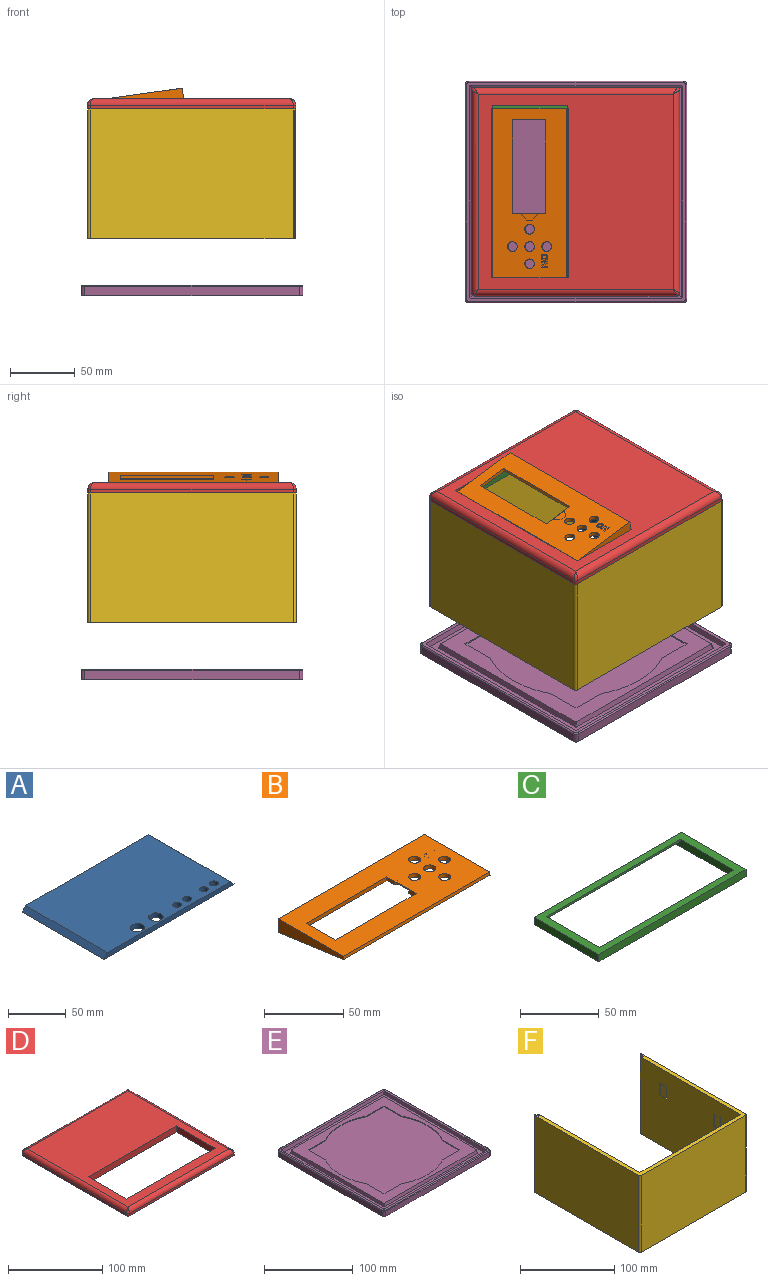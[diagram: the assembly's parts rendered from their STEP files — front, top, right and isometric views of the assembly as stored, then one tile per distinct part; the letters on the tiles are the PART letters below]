
ASSEMBLY  parts=6 mates=5
PART A: 20 faces, bbox 159.9x100x5 mm
  f0: plane 158.7x100mm, normal (0,0,-1), area 15455.6mm2, adj f2,f3,f4,f6,f8,f9,f10,f11
  f1: plane 150.52x100mm, normal (0,0,1), area 14637.8mm2, adj f3,f4,f5,f7,f8,f9,f10,f11
  f2: cylinder r=1mm len=100mm, axis (0,-1,0), area 68.3mm2, adj f0,f3,f4,f7
  f3: plane 159.91x4.98mm, normal (0,1,0), area 774.5mm2, adj f0,f1,f2,f5,f6,f7
  f4: plane 159.91x4.98mm, normal (0,-1,0), area 774.5mm2, adj f0,f1,f2,f5,f6,f7
  f5: plane 100x4.69mm, normal (-0.71,0,0.71), area 663.9mm2, adj f1,f3,f4,f6
  f6: cylinder r=1mm len=100mm, axis (0,-1,0), area 68.3mm2, adj f0,f3,f4,f5
  f7: plane 100x4.69mm, normal (0.71,0,0.71), area 663.9mm2, adj f1,f2,f3,f4
  f8: cylinder r=3.72mm len=7.44mm, axis (0,0,-1), area 116.4mm2, adj f0,f1
  f9: plane 5.37x4.98mm, normal (0,-1,0), area 26.7mm2, adj f0,f1,f10,f12
  f10: cylinder r=6.3mm len=11.4mm, axis (0,0,-1), area 71mm2, adj f0,f1,f9,f11
  f11: plane 5.37x4.98mm, normal (0,1,0), area 26.7mm2, adj f0,f1,f10,f12
  f12: cylinder r=6.3mm len=11.4mm, axis (0,0,-1), area 71mm2, adj f0,f1,f9,f11
  f13: plane 5.37x4.98mm, normal (0,1,0), area 26.7mm2, adj f0,f1,f14,f16
  f14: cylinder r=6.3mm len=11.4mm, axis (0,0,-1), area 71mm2, adj f0,f1,f13,f15
  f15: plane 5.37x4.98mm, normal (0,-1,0), area 26.7mm2, adj f0,f1,f14,f16
  f16: cylinder r=6.3mm len=11.4mm, axis (0,0,-1), area 71mm2, adj f0,f1,f13,f15
  f17: cylinder r=3.72mm len=7.44mm, axis (0,0,-1), area 116.4mm2, adj f0,f1
  f18: cylinder r=3.72mm len=7.44mm, axis (0,0,-1), area 116.4mm2, adj f0,f1
  f19: cylinder r=3.72mm len=7.44mm, axis (0,0,-1), area 116.4mm2, adj f0,f1
PART B: 69 faces, bbox 130.7x58.8x10.5 mm
  f0: plane 122.65x49.1mm, normal (0,0,-1), area 3728.6mm2, adj f3,f4,f5,f6,f7,f8,f9,f10
  f1: plane 58.44x10.54mm, normal (1,0,0), area 376.1mm2, adj f2,f17,f57,f59,f60,f61
  f2: plane 130.65x7.55mm, normal (0,1,0), area 986.6mm2, adj f1,f17,f56,f61
  f3: plane 49.1x6.97mm, normal (1,0,0), area 173.6mm2, adj f0,f4,f7,f57
  f4: plane 122.65x6.97mm, normal (0,-1,0), area 854.9mm2, adj f0,f3,f5,f57
  f5: plane 6.97x1mm, normal (-1,0,0), area 6.9mm2, adj f0,f4,f6,f57
  f6: plane 48.1x6.83mm, normal (-1,0,0), area 166.7mm2, adj f0,f5,f7,f57
  f7: plane 122.65x0.1mm, normal (0,1,0), area 12.2mm2, adj f0,f3,f6,f57
  f8: plane 25.98x3mm, normal (-1,0,0), area 43.8mm2, adj f0,f10,f16,f17,f18,f19,f22
  f9: plane 25.98x3mm, normal (1,0,0), area 77.9mm2, adj f0,f10,f16,f17
  f10: plane 71.93x3mm, normal (0,-1,0), area 215.8mm2, adj f0,f8,f9,f17
  f11: cylinder r=3.75mm len=7.5mm, axis (0,0,1), area 70.7mm2, adj f0,f17
  f12: cylinder r=3.75mm len=7.5mm, axis (0,0,1), area 70.7mm2, adj f0,f17
  f13: cylinder r=3.75mm len=7.5mm, axis (0,0,1), area 70.7mm2, adj f0,f17
  f14: cylinder r=3.75mm len=7.5mm, axis (0,0,1), area 70.7mm2, adj f0,f17
  f15: cylinder r=3.75mm len=7.5mm, axis (0,0,1), area 70.7mm2, adj f0,f17
  f16: plane 71.93x3mm, normal (0,1,0), area 215.8mm2, adj f0,f8,f9,f17
  f17: plane 130.65x58.1mm, normal (0,0,1), area 5501.1mm2, adj f1,f2,f8,f9,f10,f11,f12,f13
  f18: plane 2.5x0.5mm, normal (-0.66,-0.75,0), area 1.7mm2, adj f0,f8,f21,f22
  f19: plane 5.2x4.43mm, normal (-0.65,0.76,0), area 17.1mm2, adj f0,f8,f20,f22
  f20: plane 4.8x2.5mm, normal (-1,0,0), area 12mm2, adj f0,f19,f21,f22
  f21: plane 4.7x4mm, normal (-0.65,-0.76,0), area 15.4mm2, adj f0,f18,f20,f22
  f22: plane 13.67x5.2mm, normal (0,0,-1), area 48mm2, adj f8,f18,f19,f20,f21
  f23: cylinder r=6.23mm len=12.46mm, axis (0,0,-1), area 58.7mm2, adj f0,f24
  f24: plane 12.46x12.46mm, normal (0,0,-1), area 88.2mm2, adj f23,f26,f27,f28,f29,f30,f31,f32
  f25: plane 4.96x4.4mm, normal (0,0,-1), area 13.9mm2, adj f26,f27,f28,f29,f30,f31,f32,f33
  f26: plane 2.33x1mm, normal (-1,0,0), area 2.3mm2, adj f24,f25,f27,f37
  f27: plane 1x0.94mm, normal (0,1,0), area 0.9mm2, adj f24,f25,f26,f28
  f28: plane 4.96x1mm, normal (1,0,0), area 5mm2, adj f24,f25,f27,f29
  f29: plane 1.33x1mm, normal (0,-1,0), area 1.3mm2, adj f24,f25,f28,f30
  f30: plane 3.71x2.15mm, normal (-0.87,-0.5,0), area 4.3mm2, adj f24,f25,f29,f38
  f31: plane 3.75x2.16mm, normal (0.87,0.5,0), area 4.3mm2, adj f24,f25,f35,f36
  f32: plane 2.35x1mm, normal (1,0,0), area 2.3mm2, adj f24,f25,f33,f39
  f33: plane 1x0.95mm, normal (0,-1,0), area 0.9mm2, adj f24,f25,f32,f34
  f34: plane 4.96x1mm, normal (-1,0,0), area 5mm2, adj f24,f25,f33,f35
  f35: plane 1.34x1mm, normal (0,1,0), area 1.3mm2, adj f24,f25,f31,f34
  f36: plane 1x0.03mm, normal (0,1,0), area 0mm2, adj f24,f25,f31,f37
  f37: extruded ~1.42x1mm, area 1.4mm2, adj f24,f25,f26,f36
  f38: plane 1x0.02mm, normal (0,-1,0), area 0mm2, adj f24,f25,f30,f39
  f39: extruded ~1.37x1mm, area 1.4mm2, adj f24,f25,f32,f38
  f40: extruded ~1x0.94mm, area 1.1mm2, adj f41,f45,f46,f55
  f41: extruded ~1.67x1.26mm, area 2.4mm2, adj f40,f42,f46,f55
  f42: extruded ~1.67x1.25mm, area 2.4mm2, adj f41,f43,f46,f55
  f43: extruded ~1x0.95mm, area 1.1mm2, adj f42,f44,f46,f55
  f44: extruded ~1.25x1mm, area 1.3mm2, adj f43,f45,f46,f55
  f45: extruded ~1.25x1mm, area 1.3mm2, adj f40,f44,f46,f55
  f46: plane 5.1x4.72mm, normal (0,0,-1), area 12.9mm2, adj f40,f41,f42,f43,f44,f45,f47,f48
  f47: extruded ~1.75x1mm, area 1.9mm2, adj f24,f46,f48,f54
  f48: extruded ~1.75x1mm, area 1.9mm2, adj f24,f46,f47,f49
  f49: extruded ~1.9x1mm, area 2mm2, adj f24,f46,f48,f50
  f50: extruded ~1.89x1mm, area 2mm2, adj f24,f46,f49,f51
  f51: extruded ~1.75x1mm, area 1.9mm2, adj f24,f46,f50,f52
  f52: extruded ~1.75x1mm, area 1.9mm2, adj f24,f46,f51,f53
  f53: extruded ~1.89x1mm, area 2mm2, adj f24,f46,f52,f54
  f54: extruded ~1.89x1mm, area 2mm2, adj f24,f46,f47,f53
  f55: plane 3.35x2.52mm, normal (0,0,-1), area 7mm2, adj f40,f41,f42,f43,f44,f45
  f56: plane 58.76x10.53mm, normal (-1,0,0), area 376.5mm2, adj f2,f17,f57,f58,f60,f61
  f57: plane 130.65x58.43mm, normal (0,-0.14,-0.99), area 1627.4mm2, adj f1,f3,f4,f5,f6,f7,f56,f58
  f58: plane 130.65x2.35mm, normal (0,-0.99,0.14), area 310.5mm2, adj f17,f56,f57,f59
  f59: plane 2.41x0.34mm, normal (1,0,0), area 0.4mm2, adj f1,f57,f58
  f60: plane 130.65x2.35mm, normal (0,0.99,-0.14), area 310.5mm2, adj f1,f56,f57,f61
  f61: plane 130.65x0.62mm, normal (0,0.88,0.47), area 92.3mm2, adj f1,f2,f56,f60
  f62: plane 5.02x5mm, normal (0,1,0), area 25.1mm2, adj f0,f63,f65,f67
  f63: plane 6.75x5mm, normal (-1,0,0), area 33.8mm2, adj f0,f62,f64,f67
  f64: plane 5.02x5mm, normal (0,-1,0), area 25.1mm2, adj f0,f63,f65,f67
  f65: plane 6.75x5mm, normal (1,0,0), area 33.8mm2, adj f0,f62,f64,f67
  f66: cylinder r=1mm len=5mm, axis (0,0,1), area 31.4mm2, adj f67,f68
  f67: plane 6.75x5.02mm, normal (0,0,-1), area 30.8mm2, adj f62,f63,f64,f65,f66
  f68: plane 2x2mm, normal (0,0,-1), area 3.1mm2, adj f66
PART C: 13 faces, bbox 132.7x58.1x5.6 mm
  f0: plane 58.1x6mm, normal (0,0,-1), area 348.6mm2, adj f5,f6,f7,f8
  f1: plane 120.65x1.62mm, normal (0,-1,0), area 195.8mm2, adj f2,f8,f9,f12
  f2: plane 58.1x5.62mm, normal (-1,0,0), area 290.5mm2, adj f1,f3,f9,f10,f11,f12
  f3: plane 120.65x1.62mm, normal (0,1,0), area 195.8mm2, adj f2,f8,f9,f11
  f4: plane 58.1x5.62mm, normal (1,0,0), area 326.7mm2, adj f5,f7,f9,f10
  f5: plane 132.65x5.62mm, normal (0,1,0), area 745.9mm2, adj f0,f4,f6,f9,f10,f12
  f6: plane 58.1x5.62mm, normal (-1,0,0), area 326.7mm2, adj f0,f5,f7,f9
  f7: plane 132.65x5.62mm, normal (0,-1,0), area 745.9mm2, adj f0,f4,f6,f9,f10,f11
  f8: plane 58.1x5.62mm, normal (1,0,0), area 290.5mm2, adj f0,f1,f3,f9,f11,f12
  f9: plane 132.65x58.1mm, normal (0,0,1), area 1903.7mm2, adj f1,f2,f3,f4,f5,f6,f7,f8
  f10: plane 58.1x6mm, normal (0,0,-1), area 348.6mm2, adj f2,f4,f5,f7
  f11: plane 120.65x5mm, normal (0,0.62,-0.78), area 772.5mm2, adj f2,f3,f7,f8
  f12: plane 120.65x5mm, normal (0,-0.62,-0.78), area 772.5mm2, adj f1,f2,f5,f8
PART D: 22 faces, bbox 160.5x160.5x8 mm
  f0: plane 156.46x3mm, normal (1,0,0), area 469.4mm2, adj f1,f11,f13,f18
  f1: cylinder r=2mm len=3mm, axis (0,0,-1), area 9.4mm2, adj f0,f2,f13,f20
  f2: plane 156.46x3mm, normal (0,1,0), area 469.4mm2, adj f1,f3,f13,f21
  f3: cylinder r=2mm len=3mm, axis (0,0,-1), area 9.4mm2, adj f2,f4,f13,f19
  f4: plane 156.46x3mm, normal (-1,0,0), area 469.4mm2, adj f3,f5,f13,f17
  f5: cylinder r=2mm len=3mm, axis (0,0,-1), area 9.4mm2, adj f4,f6,f13,f15
  f6: plane 156.46x3mm, normal (0,-1,0), area 469.4mm2, adj f5,f11,f13,f14
  f7: plane 132.65x8mm, normal (0,-1,0), area 1061.2mm2, adj f8,f10,f12,f13
  f8: plane 58.1x8mm, normal (-1,0,0), area 464.8mm2, adj f7,f9,f12,f13
  f9: plane 132.65x8mm, normal (0,1,0), area 1061.2mm2, adj f8,f10,f12,f13
  f10: plane 58.1x8mm, normal (1,0,0), area 464.8mm2, adj f7,f9,f12,f13
  f11: cylinder r=2mm len=3mm, axis (0,0,-1), area 9.4mm2, adj f0,f6,f13,f16
  f12: plane 150.46x150.46mm, normal (0,0,1), area 14931.7mm2, adj f7,f8,f9,f10,f14,f17,f18,f21
  f13: plane 160.46x160.46mm, normal (0,0,-1), area 18037.5mm2, adj f0,f1,f2,f3,f4,f5,f6,f7
  f14: cylinder r=5mm len=156.46mm, axis (-1,0,0), area 1211.7mm2, adj f6,f12,f15,f16
  f15: bspline ~5.91x5mm, area 16.7mm2, adj f5,f14,f17
  f16: bspline ~5.91x5mm, area 16.7mm2, adj f11,f14,f18
  f17: cylinder r=5mm len=156.46mm, axis (0,1,0), area 1211.7mm2, adj f4,f12,f15,f19
  f18: cylinder r=5mm len=156.46mm, axis (0,-1,0), area 1211.7mm2, adj f0,f12,f16,f20
  f19: bspline ~5.91x5mm, area 16.7mm2, adj f3,f17,f21
  f20: bspline ~5.91x5mm, area 16.7mm2, adj f1,f18,f21
  f21: cylinder r=5mm len=156.46mm, axis (1,0,0), area 1211.7mm2, adj f2,f12,f19,f20
PART E: 49 faces, bbox 171.5x171.5x8.1 mm
  f0: plane 169x169mm, normal (0,0,1), area 1662.4mm2, adj f25,f26,f27,f28,f29,f30,f31,f32
  f1: plane 165x7mm, normal (0,1,0), area 1155mm2, adj f5,f29,f45,f47
  f2: plane 165x7mm, normal (-1,0,0), area 1155mm2, adj f5,f30,f43,f45
  f3: plane 165x7mm, normal (0,-1,0), area 1155mm2, adj f5,f32,f41,f43
  f4: plane 165x7mm, normal (1,0,0), area 1155mm2, adj f5,f31,f41,f47
  f5: plane 171x171mm, normal (0,0,-1), area 29233.3mm2, adj f1,f2,f3,f4,f41,f43,f45,f47
  f6: plane 162x162mm, normal (0,0,1), area 3744mm2, adj f21,f22,f23,f24,f25,f26,f27,f28
  f7: cylinder r=69mm len=66.36mm, axis (0,0,-1), area 69.2mm2, adj f8,f18,f19,f20
  f8: plane 27.32x1mm, normal (-1,0,0), area 27.3mm2, adj f7,f9,f19,f20
  f9: plane 27.32x1mm, normal (0,1,0), area 27.3mm2, adj f8,f10,f19,f20
  f10: cylinder r=69mm len=66.36mm, axis (0,0,-1), area 69.2mm2, adj f9,f11,f19,f20
  f11: plane 27.32x1mm, normal (0,1,0), area 27.3mm2, adj f10,f12,f19,f20
  f12: plane 27.32x1mm, normal (1,0,0), area 27.3mm2, adj f11,f13,f19,f20
  f13: cylinder r=69mm len=66.36mm, axis (0,0,-1), area 69.2mm2, adj f12,f14,f19,f20
  f14: plane 27.32x1mm, normal (1,0,0), area 27.3mm2, adj f13,f15,f19,f20
  f15: plane 27.32x1mm, normal (0,-1,0), area 27.3mm2, adj f14,f16,f19,f20
  f16: cylinder r=69mm len=66.36mm, axis (0,0,-1), area 69.2mm2, adj f15,f17,f19,f20
  f17: plane 27.32x1mm, normal (0,-1,0), area 27.3mm2, adj f16,f18,f19,f20
  f18: plane 27.32x1mm, normal (-1,0,0), area 27.3mm2, adj f7,f17,f19,f20
  f19: plane 148x148mm, normal (0,0,1), area 5738.6mm2, adj f7,f8,f9,f10,f11,f12,f13,f14
  f20: plane 138x138mm, normal (0,0,1), area 16164.6mm2, adj f7,f8,f9,f10,f11,f12,f13,f14
  f21: plane 148.06x4mm, normal (-0.97,0,0.24), area 606.3mm2, adj f6,f19,f37,f38
  f22: plane 148.06x4mm, normal (0,0.97,0.24), area 606.3mm2, adj f6,f19,f37,f39
  f23: plane 148.06x4mm, normal (0,-0.97,0.24), area 606.3mm2, adj f6,f19,f38,f40
  f24: plane 148.06x4mm, normal (0.97,0,0.24), area 606.3mm2, adj f6,f19,f39,f40
  f25: plane 162.06x4mm, normal (-0.97,0,0.24), area 664.1mm2, adj f0,f6,f33,f34
  f26: plane 162.06x4mm, normal (0,-0.97,0.24), area 664.1mm2, adj f0,f6,f33,f35
  f27: plane 162.06x4mm, normal (0,0.97,0.24), area 664.1mm2, adj f0,f6,f34,f36
  f28: plane 162.06x4mm, normal (0.97,0,0.24), area 664.1mm2, adj f0,f6,f35,f36
  f29: cylinder r=1mm len=165mm, axis (1,0,0), area 259.2mm2, adj f0,f1,f46,f48
  f30: cylinder r=1mm len=165mm, axis (0,1,0), area 259.2mm2, adj f0,f2,f44,f46
  f31: cylinder r=1mm len=165mm, axis (0,-1,0), area 259.2mm2, adj f0,f4,f42,f48
  f32: cylinder r=1mm len=165mm, axis (-1,0,0), area 259.2mm2, adj f0,f3,f42,f44
  f33: cylinder r=1mm len=4.18mm, axis (-0.24,-0.24,-0.94), area 6.4mm2, adj f0,f6,f25,f26
  f34: cylinder r=1mm len=4.18mm, axis (-0.24,0.24,-0.94), area 6.4mm2, adj f0,f6,f25,f27
  f35: cylinder r=1mm len=4.18mm, axis (-0.24,0.24,0.94), area 6.4mm2, adj f0,f6,f26,f28
  f36: cylinder r=1mm len=4.18mm, axis (-0.24,-0.24,0.94), area 6.4mm2, adj f0,f6,f27,f28
  f37: cylinder r=1mm len=4.18mm, axis (-0.24,0.24,-0.94), area 6.4mm2, adj f6,f19,f21,f22
  f38: cylinder r=1mm len=4.18mm, axis (-0.24,-0.24,-0.94), area 6.4mm2, adj f6,f19,f21,f23
  f39: cylinder r=1mm len=4.18mm, axis (-0.24,-0.24,0.94), area 6.4mm2, adj f6,f19,f22,f24
  f40: cylinder r=1mm len=4.18mm, axis (-0.24,0.24,0.94), area 6.4mm2, adj f6,f19,f23,f24
  f41: cylinder r=3mm len=7mm, axis (0,0,1), area 33mm2, adj f3,f4,f5,f42
  f42: torus R=2mm, axis (0,0,1), area 6.5mm2, adj f0,f31,f32,f41
  f43: cylinder r=3mm len=7mm, axis (0,0,-1), area 33mm2, adj f2,f3,f5,f44
  f44: torus R=2mm, axis (0,0,1), area 6.5mm2, adj f0,f30,f32,f43
  f45: cylinder r=3mm len=7mm, axis (0,0,1), area 33mm2, adj f1,f2,f5,f46
  f46: torus R=2mm, axis (0,0,1), area 6.5mm2, adj f0,f29,f30,f45
  f47: cylinder r=3mm len=7mm, axis (0,0,-1), area 33mm2, adj f1,f4,f5,f48
  f48: torus R=2mm, axis (0,0,1), area 6.5mm2, adj f0,f29,f31,f47
PART F: 55 faces, bbox 160.5x159.9x100 mm
  f0: plane 100x1.6mm, normal (0,1,0), area 160mm2, adj f1,f22,f23,f24
  f1: plane 100x1.7mm, normal (1,0,0), area 170mm2, adj f0,f2,f23,f24
  f2: plane 100x1.7mm, normal (1,0,0), area 170mm2, adj f1,f3,f23,f24
  f3: plane 100x1.69mm, normal (-0.71,0.71,0), area 239.6mm2, adj f2,f4,f23,f24
  f4: plane 150.5x100mm, normal (-1,0,0), area 14730mm2, adj f3,f5,f23,f24,f25,f26,f27,f29
  f5: plane 150.52x100mm, normal (0,1,0), area 14732.4mm2, adj f4,f6,f23,f24,f33,f34,f35,f37
  f6: plane 150.5x100mm, normal (1,0,0), area 14730mm2, adj f5,f7,f23,f24,f41,f42,f43,f45
  f7: plane 100x1.69mm, normal (0.71,0.71,0), area 239.6mm2, adj f6,f8,f23,f24
  f8: plane 100x1.7mm, normal (-1,0,0), area 170mm2, adj f7,f9,f23,f24
  f9: plane 100x1.55mm, normal (-1,0,0), area 155mm2, adj f8,f10,f23,f24
  f10: plane 100x0.15mm, normal (-1,0,0), area 15mm2, adj f9,f11,f23,f24
  f11: plane 100x1.6mm, normal (0,1,0), area 160mm2, adj f10,f12,f23,f24
  f12: plane 100x5mm, normal (1,0,0), area 500mm2, adj f11,f13,f23,f24
  f13: plane 100x1.1mm, normal (0.71,0.71,0), area 155.7mm2, adj f12,f14,f23,f24
  f14: cylinder r=2mm len=100mm, axis (0,0,1), area 157.2mm2, adj f13,f15,f23,f24
  f15: plane 156.46x100mm, normal (-1,0,0), area 15646mm2, adj f14,f16,f23,f24
  f16: cylinder r=2mm len=100mm, axis (0,0,1), area 314.2mm2, adj f15,f17,f23,f24
  f17: plane 156.49x100mm, normal (0,-1,0), area 15648.8mm2, adj f16,f18,f23,f24
  f18: cylinder r=2mm len=100mm, axis (0,0,1), area 314.2mm2, adj f17,f19,f23,f24
  f19: plane 156.46x100mm, normal (1,0,0), area 15646.2mm2, adj f18,f20,f23,f24
  f20: cylinder r=2mm len=100mm, axis (0,0,1), area 157.1mm2, adj f19,f21,f23,f24
  f21: plane 100x1.1mm, normal (-0.71,0.71,0), area 155.8mm2, adj f20,f22,f23,f24
  f22: plane 100x5mm, normal (-1,0,0), area 500mm2, adj f0,f21,f23,f24
  f23: plane 160.49x159.88mm, normal (0,0,1), area 2307.7mm2, adj f0,f1,f2,f3,f4,f5,f6,f7
  f24: plane 160.49x159.88mm, normal (0,0,-1), area 2307.7mm2, adj f0,f1,f2,f3,f4,f5,f6,f7
  f25: plane 16x1mm, normal (0,1,0), area 15.5mm2, adj f4,f27,f28,f52
  f26: plane 16x1mm, normal (0,-1,0), area 15.5mm2, adj f4,f27,f28,f52
  f27: plane 10x1mm, normal (0,0,1), area 10mm2, adj f4,f25,f26,f28
  f28: plane 15x10mm, normal (-1,0,0), area 150mm2, adj f25,f26,f27,f52
  f29: plane 16x1mm, normal (0,1,0), area 15.5mm2, adj f4,f31,f32,f54
  f30: plane 16x1mm, normal (0,-1,0), area 15.5mm2, adj f4,f31,f32,f54
  f31: plane 10x1mm, normal (0,0,1), area 10mm2, adj f4,f29,f30,f32
  f32: plane 15x10mm, normal (-1,0,0), area 150mm2, adj f29,f30,f31,f54
  f33: plane 16x1mm, normal (1,0,0), area 15.5mm2, adj f5,f35,f36,f51
  f34: plane 16x1mm, normal (-1,0,0), area 15.5mm2, adj f5,f35,f36,f51
  f35: plane 10x1mm, normal (0,0,1), area 10mm2, adj f5,f33,f34,f36
  f36: plane 15x10mm, normal (0,1,0), area 150mm2, adj f33,f34,f35,f51
  f37: plane 16x1mm, normal (1,0,0), area 15.5mm2, adj f5,f39,f40,f53
  f38: plane 16x1mm, normal (-1,0,0), area 15.5mm2, adj f5,f39,f40,f53
  f39: plane 10x1mm, normal (0,0,1), area 10mm2, adj f5,f37,f38,f40
  f40: plane 15x10mm, normal (0,1,0), area 150mm2, adj f37,f38,f39,f53
  f41: plane 16x1mm, normal (0,-1,0), area 15.5mm2, adj f6,f43,f44,f49
  f42: plane 16x1mm, normal (0,1,0), area 15.5mm2, adj f6,f43,f44,f49
  f43: plane 10x1mm, normal (0,0,1), area 10mm2, adj f6,f41,f42,f44
  f44: plane 15x10mm, normal (1,0,0), area 150mm2, adj f41,f42,f43,f49
  f45: plane 16x1mm, normal (0,-1,0), area 15.5mm2, adj f6,f47,f48,f50
  f46: plane 16x1mm, normal (0,1,0), area 15.5mm2, adj f6,f47,f48,f50
  f47: plane 10x1mm, normal (0,0,1), area 10mm2, adj f6,f45,f46,f48
  f48: plane 15x10mm, normal (1,0,0), area 150mm2, adj f45,f46,f47,f50
  f49: plane 10x1mm, normal (0.71,0,-0.71), area 14.1mm2, adj f6,f41,f42,f44
  f50: plane 10x1mm, normal (0.71,0,-0.71), area 14.1mm2, adj f6,f45,f46,f48
  f51: plane 10x1mm, normal (0,0.71,-0.71), area 14.1mm2, adj f5,f33,f34,f36
  f52: plane 10x1mm, normal (-0.71,0,-0.71), area 14.1mm2, adj f4,f25,f26,f28
  f53: plane 10x1mm, normal (0,0.71,-0.71), area 14.1mm2, adj f5,f37,f38,f40
  f54: plane 10x1mm, normal (-0.71,0,-0.71), area 14.1mm2, adj f4,f29,f30,f32
PLACE A rot(axis=(-0.58,-0.58,0.58),120deg) t=(297.84,-22.46,117.04)mm
PLACE B rot(axis=(0.07,-0.07,-1),90.3deg) t=(182.03,-23.47,175.4)mm
PLACE C rot(axis=(0,0,-1),90deg) t=(222.59,-22.46,167.04)mm
PLACE D rot(axis=(0,0,-1),90deg) t=(222.59,-22.46,167.04)mm
PLACE E t=(222.86,-22.46,23.04)mm
PLACE F rot(axis=(0,0,-1),90deg) t=(222.59,-22.45,67.04)mm
MATE fastened A.f4 <-> D.f13  axis (0,0,1) through (302.82,-22.46,167.04)mm
MATE parallel D.f12 <-> E.f10  axis (0,0,1) through (240.86,-22.46,175.04)mm
MATE fastened C.f7 <-> D.f9  axis (-1,0,0) through (158.13,-88.79,167.04)mm
MATE fastened B.f57 <-> C.f9  axis (0,0,-1) through (158.13,-88.79,172.66)mm
MATE fastened D.f11 <-> F.f18  axis (0,0,-1) through (144.36,-100.69,167.04)mm
